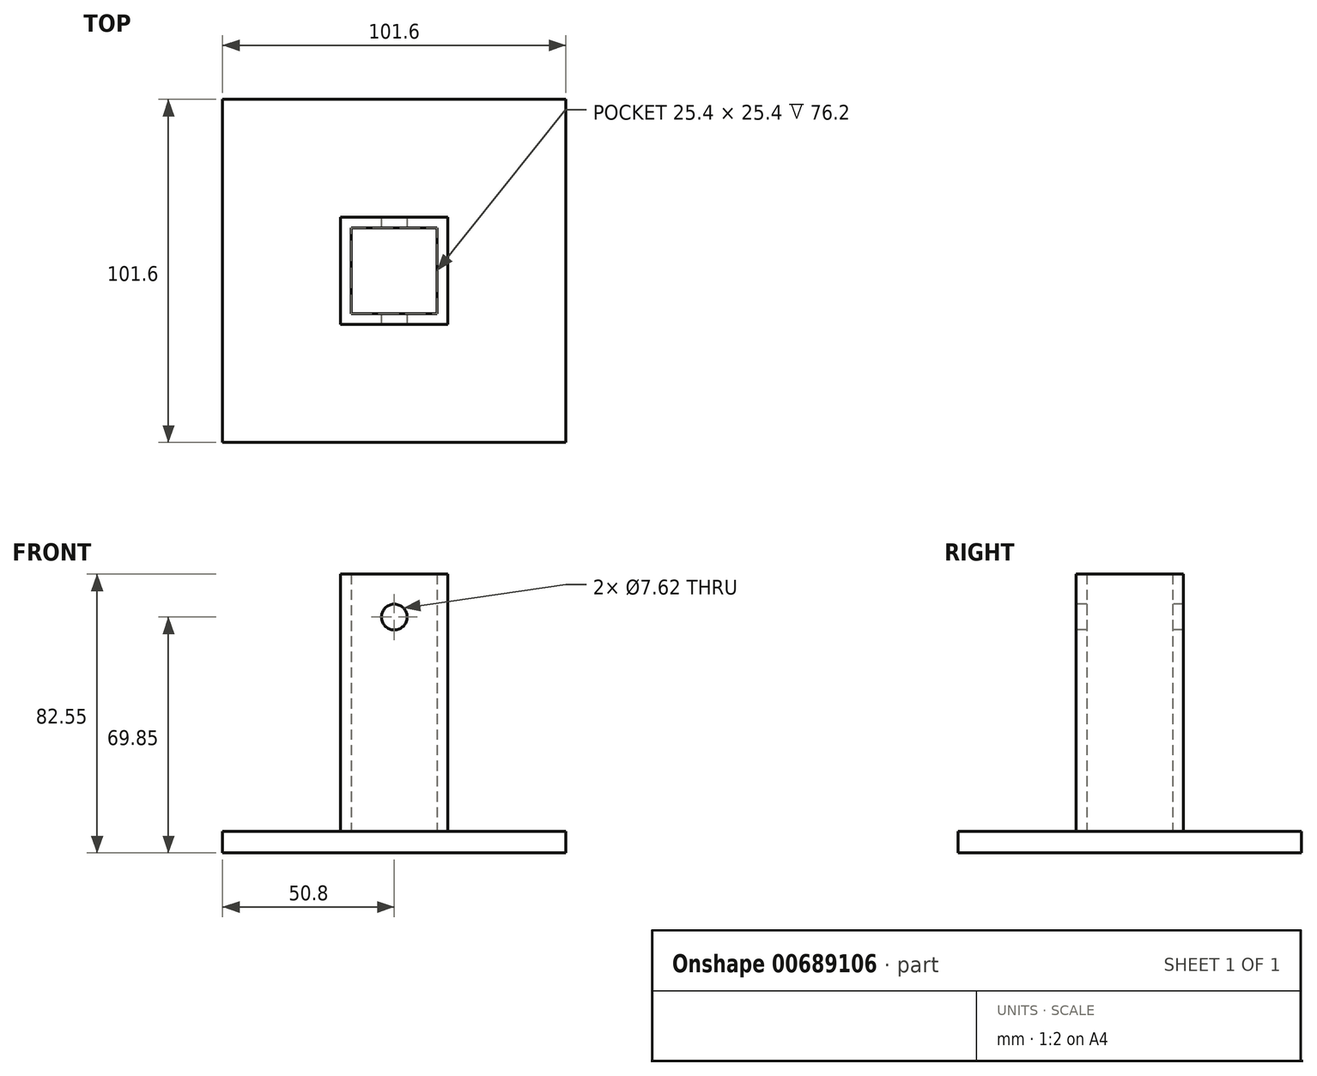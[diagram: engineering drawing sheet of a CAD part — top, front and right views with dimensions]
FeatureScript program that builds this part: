
annotation { "Feature Type Name" : "Feature", "Feature Type Description" : "" }
export const myFeature = defineFeature(function(context is Context, id is Id, definition is map)
    precondition{}
    {
        {
            var Q0;
            Q0=qCreatedBy(makeId("Top.planeOp"),FACE);
            var sketch = newSketch(context, id + "F0", { "sketchPlane" : qUnion([Q0])});
            skLineSegment(sketch, "E0.bottom", {"start": v(-50.8, 50.8) * mm, "end": v(50.8, 50.8) * mm});
            skLineSegment(sketch, "E0.top", {"start": v(-50.8, -50.8) * mm, "end": v(50.8, -50.8) * mm});
            skLineSegment(sketch, "E0.left", {"start": v(-50.8, 50.8) * mm, "end": v(-50.8, -50.8) * mm});
            skLineSegment(sketch, "E0.right", {"start": v(50.8, 50.8) * mm, "end": v(50.8, -50.8) * mm});
            skSolve(sketch);
        }
        {
            var Q0;
            Q0=makeQuery(id+"F0.imprint","IMPRINT",FACE,{"disambiguationData":[TD([[makeQuery(id+"F0.imprint","IMPRINT",EDGE,{"derivedFrom":sQuery(id+"F0.wireOp",EDGE,"E0.bottom")}),-1.0]])]});
            extrude(context, id + "F1", {"entities" : qUnion([Q0]), "depth" : 6.35 * mm, "offsetDistance" : 25.4 * mm});
        }
        {
            var Q0;
            Q0=makeQuery(id+"F1.opExtrude","CAP_FACE",FACE,{"disambiguationData":[OSD([sQuery(id+"F0.wireOp",EDGE,"E0.bottom"),sQuery(id+"F0.wireOp",EDGE,"E0.top"),sQuery(id+"F0.wireOp",EDGE,"E0.left"),sQuery(id+"F0.wireOp",EDGE,"E0.right")])],"isStart":false});
            var sketch = newSketch(context, id + "F2", { "sketchPlane" : qUnion([Q0])});
            skLineSegment(sketch, "E1.bottom", {"start": v(-15.88, 15.88) * mm, "end": v(15.88, 15.88) * mm});
            skLineSegment(sketch, "E1.top", {"start": v(-15.88, -15.88) * mm, "end": v(15.88, -15.88) * mm});
            skLineSegment(sketch, "E1.left", {"start": v(-15.88, 15.88) * mm, "end": v(-15.88, -15.88) * mm});
            skLineSegment(sketch, "E1.right", {"start": v(15.88, 15.88) * mm, "end": v(15.88, -15.88) * mm});
            skLineSegment(sketch, "E2.0", {"start": v(-12.7, 12.7) * mm, "end": v(12.7, 12.7) * mm});
            skLineSegment(sketch, "E2.1", {"start": v(-12.7, 12.7) * mm, "end": v(-12.7, -12.7) * mm});
            skLineSegment(sketch, "E2.2", {"start": v(-12.7, -12.7) * mm, "end": v(12.7, -12.7) * mm});
            skLineSegment(sketch, "E2.3", {"start": v(12.7, 12.7) * mm, "end": v(12.7, -12.7) * mm});
            skSolve(sketch);
        }
        {
            var Q0;
            Q0=makeQuery(id+"F2.imprint","IMPRINT",FACE,{"disambiguationData":[TD([[makeQuery(id+"F2.imprint","IMPRINT",EDGE,{"derivedFrom":sQuery(id+"F2.wireOp",EDGE,"E1.bottom")}),-1.0]])]});
            extrude(context, id + "F3", {"entities" : qUnion([Q0]), "operationType" : NewBodyOperationType.ADD, "depth" : 76.2 * mm, "offsetDistance" : 25.4 * mm});
        }
        {
            var Q0;
            Q0=makeQuery(id+"F3.opExtrude","SWEPT_FACE",FACE,{"disambiguationData":[OSD([sQuery(id+"F2.wireOp",EDGE,"E1.top")])]});
            var sketch = newSketch(context, id + "F4", { "sketchPlane" : qUnion([Q0])});
            skCircle(sketch, "E3", {"center": v(0, 69.85) * mm, "radius": 3.81 * mm});
            skSolve(sketch);
        }
        {
            var Q0;
            Q0=makeQuery(id+"F4.imprint","IMPRINT",FACE,{"disambiguationData":[TD([[makeQuery(id+"F4.imprint","IMPRINT",EDGE,{"derivedFrom":sQuery(id+"F4.wireOp",EDGE,"E3")}),1.0]])]});
            extrude(context, id + "F5", {"entities" : qUnion([Q0]), "operationType" : NewBodyOperationType.REMOVE, "endBound" : BoundingType.THROUGH_ALL, "oppositeDirection" : true, "depth" : 25.4 * mm, "offsetDistance" : 25.4 * mm});
        }
    });
